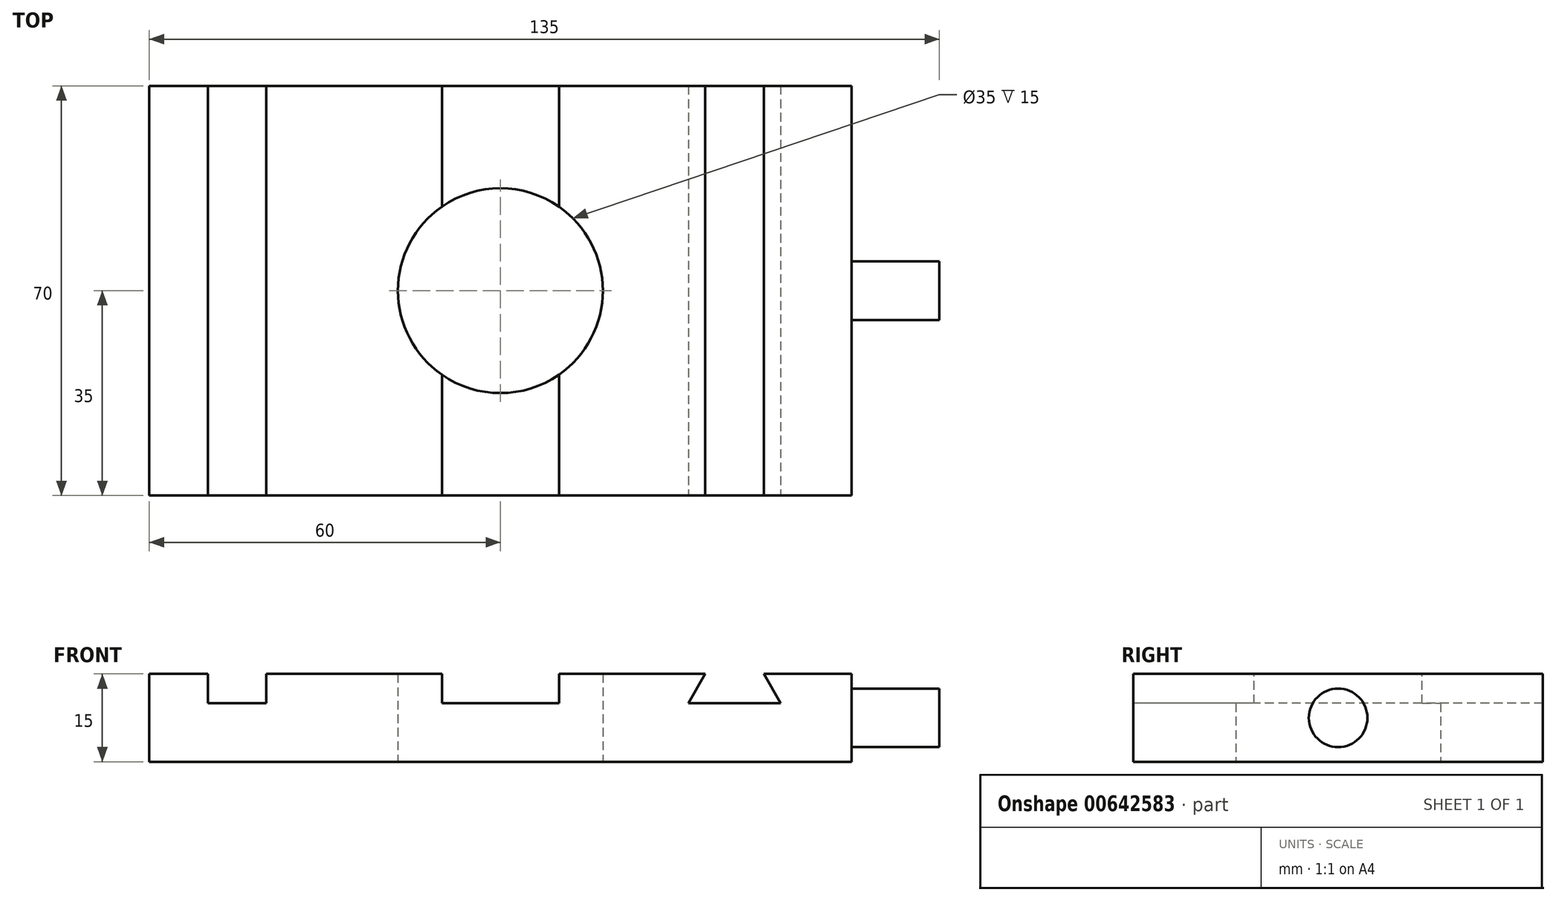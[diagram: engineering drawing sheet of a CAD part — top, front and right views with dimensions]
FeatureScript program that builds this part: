
annotation { "Feature Type Name" : "Feature", "Feature Type Description" : "" }
export const myFeature = defineFeature(function(context is Context, id is Id, definition is map)
    precondition{}
    {
        {
            var Q0;
            Q0=qCreatedBy(makeId("Top.planeOp"),FACE);
            var sketch = newSketch(context, id + "F0", { "sketchPlane" : qUnion([Q0])});
            skLineSegment(sketch, "E0.bottom", {"start": v(60, 35) * mm, "end": v(-60, 35) * mm});
            skLineSegment(sketch, "E0.top", {"start": v(60, -35) * mm, "end": v(-60, -35) * mm});
            skLineSegment(sketch, "E0.left", {"start": v(60, 35) * mm, "end": v(60, -35) * mm});
            skLineSegment(sketch, "E0.right", {"start": v(-60, 35) * mm, "end": v(-60, -35) * mm});
            skPoint(sketch, "E0.middle", {"position": v(0, 0) * mm});
            skCircle(sketch, "E1", {"center": v(0, 0) * mm, "radius": 17.5 * mm});
            skSolve(sketch);
        }
        {
            var Q0;
            Q0 = qSketchRegion(id + "F0", true);
            extrude(context, id + "F1", {"entities" : qUnion([Q0]), "depth" : 15 * mm, "offsetDistance" : 25 * mm});
        }
        {
            var Q0;
            Q0=makeQuery(id+"F1.opExtrude","CAP_FACE",FACE,{"disambiguationData":[OSD([sQuery(id+"F0.wireOp",EDGE,"E0.bottom"),sQuery(id+"F0.wireOp",EDGE,"E0.top"),sQuery(id+"F0.wireOp",EDGE,"E0.left"),sQuery(id+"F0.wireOp",EDGE,"E0.right"),sQuery(id+"F0.wireOp",EDGE,"E1")])],"isStart":false});
            var sketch = newSketch(context, id + "F2", { "sketchPlane" : qUnion([Q0])});
            skLineSegment(sketch, "E2.bottom", {"start": v(-50, 35) * mm, "end": v(-40, 35) * mm});
            skLineSegment(sketch, "E2.top", {"start": v(-50, -35) * mm, "end": v(-40, -35) * mm});
            skLineSegment(sketch, "E2.left", {"start": v(-50, 35) * mm, "end": v(-50, -35) * mm});
            skLineSegment(sketch, "E2.right", {"start": v(-40, 35) * mm, "end": v(-40, -35) * mm});
            skLineSegment(sketch, "E3", {"start": v(-10, 35) * mm, "end": v(-10, -35) * mm});
            skLineSegment(sketch, "E4", {"start": v(-10, -35) * mm, "end": v(10, -35) * mm});
            skLineSegment(sketch, "E5", {"start": v(10, -35) * mm, "end": v(10, 35) * mm});
            skLineSegment(sketch, "E6", {"start": v(0, -35) * mm, "end": v(0, 35) * mm, "construction": true});
            skSolve(sketch);
        }
        {
            var Q0;
            Q0=makeQuery(id+"F2.imprint","IMPRINT",FACE,{"disambiguationData":[TD([[makeQuery(id+"F2.imprint","IMPRINT",EDGE,{"derivedFrom":sQuery(id+"F2.wireOp",EDGE,"E2.bottom")}),1.0]])]});
            var Q1;
            {var subQ0=sQuery(id+"F2.wireOp",EDGE,"E4");Q1=makeQuery(id+"F2.imprint","IMPRINT",FACE,{"disambiguationData":[TD([[makeQuery(id+"F2.imprint","IMPRINT",EDGE,{"derivedFrom":subQ0}),-1.0]])]});}
            var Q2;
            {var subQ0=sQuery(id+"F2.wireOp",EDGE,"E3");var subQ1=makeQuery(id+"F1.opExtrude","CAP_EDGE",EDGE,{"disambiguationData":[OSD([sQuery(id+"F0.wireOp",EDGE,"E0.bottom")])],"isStart":false});var subQ2=makeQuery(id+"F2.imprint","INTERSECT",VERTEX,{"derivedFrom":[subQ1,subQ0]});Q2=makeQuery(id+"F2.imprint","IMPRINT",FACE,{"disambiguationData":[TD([[makeQuery(id+"F2.imprint","IMPRINT",EDGE,{"disambiguationData":[TD([[subQ2,-1.0]])],"derivedFrom":subQ0}),1.0]])]});}
            extrude(context, id + "F3", {"entities" : qUnion([Q0, Q1, Q2]), "operationType" : NewBodyOperationType.REMOVE, "oppositeDirection" : true, "depth" : 5 * mm, "offsetDistance" : 25 * mm});
        }
        {
            var Q0;
            Q0=makeQuery(id+"F1.opExtrude","SWEPT_FACE",FACE,{"disambiguationData":[OSD([sQuery(id+"F0.wireOp",EDGE,"E0.top")])]});
            var sketch = newSketch(context, id + "F4", { "sketchPlane" : qUnion([Q0])});
            skLineSegment(sketch, "E7", {"start": v(35, 15) * mm, "end": v(32.11, 10) * mm});
            skLineSegment(sketch, "E8", {"start": v(32.11, 10) * mm, "end": v(47.89, 10) * mm});
            skLineSegment(sketch, "E9", {"start": v(47.89, 10) * mm, "end": v(45, 15) * mm});
            skLineSegment(sketch, "E10", {"start": v(45, 15) * mm, "end": v(35, 15) * mm});
            skLineSegment(sketch, "E11", {"start": v(40, 10) * mm, "end": v(40, 15) * mm, "construction": true});
            skSolve(sketch);
        }
        {
            var Q0;
            Q0=makeQuery(id+"F4.imprint","IMPRINT",FACE,{"disambiguationData":[TD([[makeQuery(id+"F4.imprint","IMPRINT",EDGE,{"derivedFrom":sQuery(id+"F4.wireOp",EDGE,"E7")}),1.0]])]});
            extrude(context, id + "F5", {"entities" : qUnion([Q0]), "operationType" : NewBodyOperationType.REMOVE, "endBound" : BoundingType.THROUGH_ALL, "oppositeDirection" : true, "depth" : 25 * mm, "offsetDistance" : 25 * mm});
        }
        {
            var Q0;
            Q0=makeQuery(id+"F1.opExtrude","SWEPT_FACE",FACE,{"disambiguationData":[OSD([sQuery(id+"F0.wireOp",EDGE,"E0.left")])]});
            var sketch = newSketch(context, id + "F6", { "sketchPlane" : qUnion([Q0])});
            skCircle(sketch, "E12", {"center": v(0, 7.5) * mm, "radius": 5 * mm});
            skPoint(sketch, "E12.centerSnap0", {"position": v(-35, 7.5) * mm});
            skPoint(sketch, "E12.centerSnap1", {"position": v(0, 15) * mm});
            skSolve(sketch);
        }
        {
            var Q0;
            Q0 = qSketchRegion(id + "F6", true);
            extrude(context, id + "F7", {"entities" : qUnion([Q0]), "operationType" : NewBodyOperationType.ADD, "depth" : 15 * mm, "offsetDistance" : 25 * mm});
        }
    });
